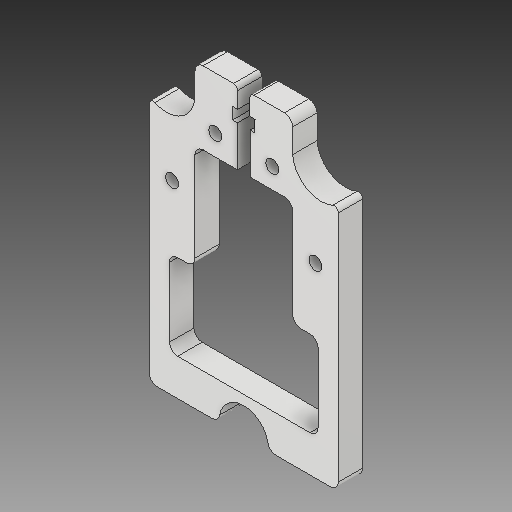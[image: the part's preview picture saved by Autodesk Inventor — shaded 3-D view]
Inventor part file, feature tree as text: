
AUTODESK INVENTOR PART (.ipt)
format: ipt  version: 2018 (Build 220112000, 112)  size: 198,144 bytes
history: native  units: mm
features: other x3, sketch x2
ambient origin geometry x8: Origin, YZ Plane, XZ Plane, XY Plane, X Axis, Y Axis, Z Axis, Center Point
bodies: Solid1 (feature_tree)
feature tree (5):
  other  "Hotend Slide Part 2.ipt"
  other  "Solid1::Hotend Slide Part 2.ipt"
  other  "TaggingFeature1"
  sketch  "Sketch1"  dims[d0=10.0mm]
  sketch  "Sketch2"
